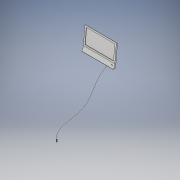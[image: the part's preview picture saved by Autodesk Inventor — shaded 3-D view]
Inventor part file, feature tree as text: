
AUTODESK INVENTOR PART (.ipt)
format: ipt  version: 2017 (Build 210142000, 142)  size: 458,752 bytes
history: native  units: in
note: dims shown in document units (in); Inventor stores cm internally (conversion verified against a paired STEP export)
features: sketch x14, extrude x12, other x8, plane x2, sweep x1, loft x1
ambient origin geometry x8: Origin, YZ Plane, XZ Plane, XY Plane, X Axis, Y Axis, Z Axis, Center Point
bodies: Solid1 (feature_tree), Solid2 (feature_tree), Solid3 (feature_tree)
feature tree (38):
  extrude  "block to cut from"  Depth=1.7188in
  extrude  "side view correct"  Depth=0.0104in
  extrude  "top view correct"  Depth=0.5841in
  plane  "Work Plane1"
  extrude  "slight top view correction"  Depth=0.0104in
  extrude  "screen"  TaperAngle=135.0deg  [1 undecoded]
  plane  "Work Plane2"
  extrude  "light cutout"  Depth=0.9583in
  sketch  "Sketch8"  dims[d17=0.0729in d19=0.1807in]
  extrude  "power indicator"  Depth=0.1807in
  extrude  "power button"  Depth=0.4271in TaperAngle=0.0deg
  extrude  "power symble"  Depth=0.3333in
  sweep  "wire"
  other  "plug bottom workplane"
  loft  "plug protection half"
  sketch  "Sketch17"  dims[d32=0.0781in d33=0.0833in]
  extrude  "hot wires"  Depth=0.0833in
  extrude  "ground wire"  Depth=0.0833in
  extrude  "addons for the hot wires"  Depth=0.3937in
  other  "ground pin round cut"
  other  "ground pin cut"
  other  "mate plane middle"
  other  "mate to back of stand"
  sketch  "Sketch1"  dims[d0=1.1771in d1=1.7188in]
  sketch  "Sketch2"  dims[d2=0.5527in d3=0.0in d4=0.0104in]
  sketch  "Sketch3"  dims[d6=0.3125in d7=0.5841in]
  sketch  "Sketch4"  dims[d8=0.6927in d12=0.0104in]
  sketch  "Sketch5"  dims[d13=0.0677in d14=135.0deg]
  sketch  "Sketch7"  dims[d15=0.1042in d16=0.9583in]
  sketch  "Sketch11"  dims[d20=5.6652in d21=0.4271in d22=0.0in]
  other  "cord line"
  sketch  "Sketch13"  dims[d23=0.3333in d24=0.3333in]
  other  "plug middle workplane"
  sketch  "Sketch15"  dims[d25=0.4271in d26=0.0in d27=90.0deg]
  sketch  "Sketch16"  dims[d28=0.0625in d29=1.4896in d30=0.0in]
  sketch  "Sketch18"  dims[d34=0.0781in d35=0.0833in]
  other  "Work Axis1"
  sketch  "Sketch19"  dims[d36=0.0208in d37=0.0in d38=0.0625in d40=45.0deg d49=0.0938in d50=0.0762in d51=0.021in d52=0.03in d53=0.0in d54=0.0749in d55=0.0013in d56=0.0185in d57=0.03in d58=0.0in d59=0.017in d60=0.0137in d61=0.0in d73=0.0019in d76=0.001in d77=0.001in d78=0.001in d79=0.0in d81=0.3827in d82=0.3937in d83=0.02in d84=0.3827in d85=0.0in d86=0.0in d87=0.0366in d88=0.0535in d89=0.0837in d92=0.0454in d93=0.0364in d97=0.0453in d111=0.3937in d130=0.0535in d131=0.0268in d132=0.0329in d133=0.0364in d134=0.0165in d135=0.0415in d136=0.0052in d137=0.0105in d139=0.0in d140=90.0deg d141=0.0in d142=90.0deg d143=0.0in d144=90.0deg d145=0.0045in d146=0.0189in d147=0.0189in d148=0.0208in d149=0.0125in d150=0.0157in d151=0.0115in d152=0.0558in d153=0.0in d154=0.0679in d155=0.0in d156=0.0064in d157=0.0047in d158=0.0098in d159=0.0141in d160=0.0679in d161=0.0in d162=90.0deg d164=0.0157in d165=90.0deg d166=0.02in]
note: 1 required parameter value undecoded (feature->parameter linkage not recoverable at this tier; creation-order binding heuristic only, values carry confidence <= 0.55)
